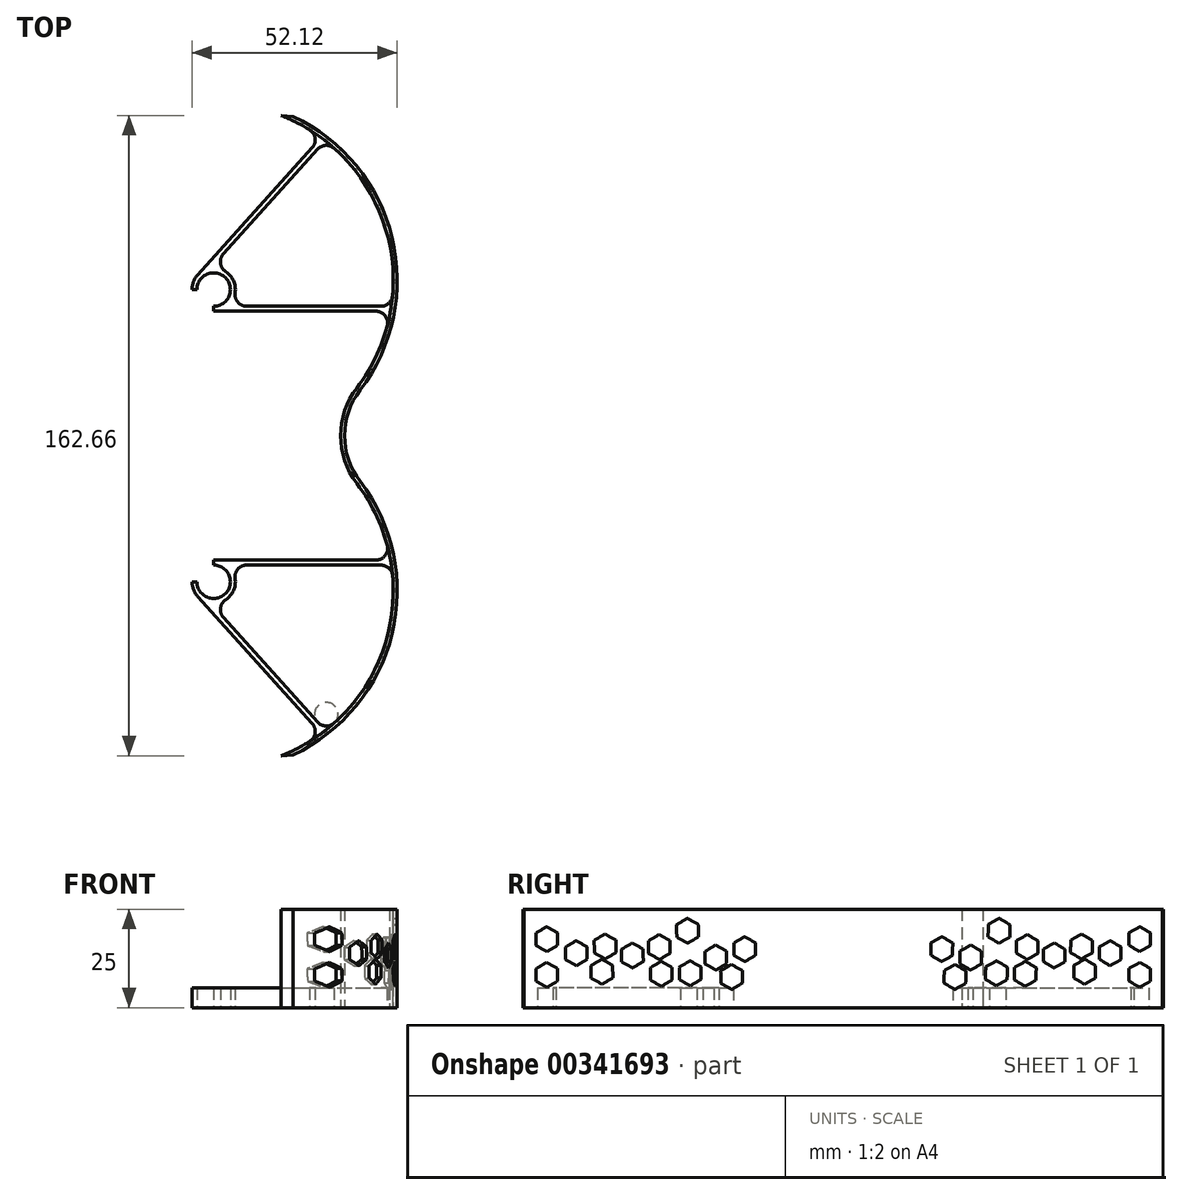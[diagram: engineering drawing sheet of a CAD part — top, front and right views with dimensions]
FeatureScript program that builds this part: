
annotation { "Feature Type Name" : "Feature", "Feature Type Description" : "" }
export const myFeature = defineFeature(function(context is Context, id is Id, definition is map)
    precondition{}
    {
        {
            var Q0;
            Q0=qCreatedBy(makeId("Top.planeOp"),FACE);
            var sketch = newSketch(context, id + "F0", { "sketchPlane" : qUnion([Q0])});
            skCircle(sketch, "E0", {"center": v(0, 0) * mm, "radius": 52.5 * mm, "construction": true});
            skLineSegment(sketch, "E1.bottom", {"start": v(-52.5, 52.5) * mm, "end": v(52.5, 52.5) * mm, "construction": true});
            skLineSegment(sketch, "E1.top", {"start": v(-52.5, -52.5) * mm, "end": v(52.5, -52.5) * mm, "construction": true});
            skLineSegment(sketch, "E1.left", {"start": v(-52.5, 52.5) * mm, "end": v(-52.5, -52.5) * mm, "construction": true});
            skLineSegment(sketch, "E1.right", {"start": v(52.5, 52.5) * mm, "end": v(52.5, -52.5) * mm, "construction": true});
            skLineSegment(sketch, "E2", {"start": v(-52.5, 52.5) * mm, "end": v(52.5, -52.5) * mm, "construction": true});
            skLineSegment(sketch, "E3", {"start": v(52.5, 52.5) * mm, "end": v(-52.5, -52.5) * mm, "construction": true});
            skCircle(sketch, "E4", {"center": v(37.12, -37.12) * mm, "radius": 33 * mm, "construction": true});
            skLineSegment(sketch, "E5.bottom", {"start": v(37.12, -37.12) * mm, "end": v(-37.12, -37.12) * mm, "construction": true});
            skLineSegment(sketch, "E5.top", {"start": v(37.12, 37.12) * mm, "end": v(-37.12, 37.12) * mm, "construction": true});
            skLineSegment(sketch, "E5.left", {"start": v(37.12, -37.12) * mm, "end": v(37.12, 37.12) * mm, "construction": true});
            skLineSegment(sketch, "E5.right", {"start": v(-37.12, -37.12) * mm, "end": v(-37.12, 37.12) * mm, "construction": true});
            skCircle(sketch, "E6", {"center": v(0, -37.12) * mm, "radius": 70 * mm, "construction": true});
            skCircle(sketch, "E7.MirrorC", {"center": v(0, 37.12) * mm, "radius": 70 * mm, "construction": true});
            skArc(sketch, "E8", {"start": v(54.28, -81.33) * mm, "mid": v(57.8, -79.76) * mm, "end": v(61.18, -77.89) * mm});
            skArc(sketch, "E9.MirrorCS", {"start": v(54.28, 81.33) * mm, "mid": v(57.8, 79.76) * mm, "end": v(61.18, 77.89) * mm});
            skPoint(sketch, "E10.visualSharp", {"position": v(59.35, 0) * mm});
            skArc(sketch, "E10.filletArc", {"start": v(73.5, 12.15) * mm, "mid": v(69.38, 0) * mm, "end": v(73.5, -12.15) * mm});
            skArc(sketch, "E11.0", {"start": v(57.33, 81.1) * mm, "mid": v(82.43, 50.37) * mm, "end": v(74.29, 11.54) * mm});
            skArc(sketch, "E11.1", {"start": v(74.29, 11.54) * mm, "mid": v(70.38, 0) * mm, "end": v(74.29, -11.54) * mm});
            skArc(sketch, "E11.2", {"start": v(57.33, -81.1) * mm, "mid": v(82.43, -50.37) * mm, "end": v(74.29, -11.54) * mm});
            skLineSegment(sketch, "E12", {"start": v(54.28, -81.33) * mm, "end": v(57.33, -81.1) * mm});
            skLineSegment(sketch, "E13.MirrorCS", {"start": v(54.28, 81.33) * mm, "end": v(57.33, 81.1) * mm});
            skArc(sketch, "E14.trimOffspring", {"start": v(81.77, -30.15) * mm, "mid": v(78.63, -20.69) * mm, "end": v(73.5, -12.15) * mm});
            skPoint(sketch, "E15.visualSharp", {"position": v(82.51, -34.92) * mm});
            skPoint(sketch, "E16.visualSharp", {"position": v(82.4, -33.91) * mm});
            skArc(sketch, "E17", {"start": v(82.7, -37.69) * mm, "mid": v(82.4, -33.9) * mm, "end": v(81.77, -30.15) * mm});
            skArc(sketch, "E18.trimOffspring", {"start": v(67.26, -73.45) * mm, "mid": v(79.05, -57.33) * mm, "end": v(82.7, -37.69) * mm});
            skPoint(sketch, "E19.visualSharp", {"position": v(64.92, -75.34) * mm});
            skPoint(sketch, "E20.visualSharp", {"position": v(64.12, -75.94) * mm});
            skArc(sketch, "E21", {"start": v(61.18, -77.89) * mm, "mid": v(64.3, -75.79) * mm, "end": v(67.26, -73.45) * mm});
            skArc(sketch, "E22.MirrorCS", {"start": v(82.7, 37.69) * mm, "mid": v(82.65, 36.65) * mm, "end": v(82.58, 35.61) * mm});
            skArc(sketch, "E23.MirrorCS", {"start": v(61.18, 77.89) * mm, "mid": v(61.35, 77.79) * mm, "end": v(61.52, 77.68) * mm});
            skLineSegment(sketch, "E24.trimOffspring", {"start": v(64.1, 75.93) * mm, "end": v(64.12, 75.94) * mm});
            skLineSegment(sketch, "E25.trimOffspring", {"start": v(82.4, 33.91) * mm, "end": v(82.4, 33.91) * mm});
            skArc(sketch, "E26", {"start": v(37.12, 32.87) * mm, "mid": v(40.13, 40.13) * mm, "end": v(32.87, 37.12) * mm});
            skLineSegment(sketch, "E27.0", {"start": v(34.73, 39.33) * mm, "end": v(34.75, 39.35) * mm});
            skArc(sketch, "E28", {"start": v(33.04, 40.8) * mm, "mid": v(31.99, 39.1) * mm, "end": v(31.62, 37.12) * mm});
            skLineSegment(sketch, "E29", {"start": v(37.12, 31.62) * mm, "end": v(78.32, 31.62) * mm});
            skLineSegment(sketch, "E30", {"start": v(45.53, 32.87) * mm, "end": v(79.59, 32.87) * mm});
            skLineSegment(sketch, "E31", {"start": v(33.04, 40.8) * mm, "end": v(62.15, 73.14) * mm});
            skLineSegment(sketch, "E32", {"start": v(39.6, 46.21) * mm, "end": v(63.51, 72.79) * mm});
            skArc(sketch, "E33.trimOffspring", {"start": v(42.56, 36.31) * mm, "mid": v(42.15, 39.36) * mm, "end": v(40.16, 41.7) * mm});
            skArc(sketch, "E34.trimOffspring", {"start": v(67.74, 73.02) * mm, "mid": v(79.18, 57.03) * mm, "end": v(82.7, 37.69) * mm});
            skArc(sketch, "E35.trimOffspring", {"start": v(81.21, 27.85) * mm, "mid": v(78.12, 19.62) * mm, "end": v(73.5, 12.15) * mm});
            skArc(sketch, "E36.filletArc", {"start": v(62.15, 73.14) * mm, "mid": v(62.89, 75.55) * mm, "end": v(61.52, 77.68) * mm});
            skPoint(sketch, "E37.visualSharp", {"position": v(65.45, 74.94) * mm});
            skArc(sketch, "E37.filletArc", {"start": v(67.74, 73.02) * mm, "mid": v(65.58, 73.78) * mm, "end": v(63.51, 72.79) * mm});
            skArc(sketch, "E38.filletArc", {"start": v(79.59, 32.87) * mm, "mid": v(81.61, 33.66) * mm, "end": v(82.58, 35.61) * mm});
            skArc(sketch, "E39.filletArc", {"start": v(81.21, 27.85) * mm, "mid": v(80.7, 30.45) * mm, "end": v(78.32, 31.62) * mm});
            skPoint(sketch, "E40.visualSharp", {"position": v(36.3, 42.56) * mm});
            skArc(sketch, "E40.filletArc", {"start": v(39.6, 46.21) * mm, "mid": v(38.84, 43.83) * mm, "end": v(40.16, 41.7) * mm});
            skPoint(sketch, "E41.visualSharp", {"position": v(40.61, 32.87) * mm});
            skArc(sketch, "E41.filletArc", {"start": v(42.56, 36.31) * mm, "mid": v(43.26, 33.91) * mm, "end": v(45.53, 32.87) * mm});
            skLineSegment(sketch, "E42.MirrorCS", {"start": v(37.12, -31.62) * mm, "end": v(78.32, -31.62) * mm});
            skLineSegment(sketch, "E43.MirrorCS", {"start": v(45.53, -32.87) * mm, "end": v(79.59, -32.87) * mm});
            skArc(sketch, "E44.MirrorCS", {"start": v(81.21, -27.85) * mm, "mid": v(80.7, -30.45) * mm, "end": v(78.32, -31.62) * mm});
            skArc(sketch, "E45.MirrorCS", {"start": v(79.59, -32.87) * mm, "mid": v(81.61, -33.66) * mm, "end": v(82.58, -35.61) * mm});
            skArc(sketch, "E46.MirrorCS", {"start": v(33.04, -40.8) * mm, "mid": v(31.99, -39.1) * mm, "end": v(31.62, -37.12) * mm});
            skArc(sketch, "E47.MirrorC", {"start": v(37.12, -32.87) * mm, "mid": v(40.13, -40.13) * mm, "end": v(32.87, -37.12) * mm});
            skArc(sketch, "E48.MirrorCS", {"start": v(42.56, -36.31) * mm, "mid": v(42.15, -39.36) * mm, "end": v(40.16, -41.7) * mm});
            skArc(sketch, "E49.MirrorCS", {"start": v(39.6, -46.21) * mm, "mid": v(38.84, -43.83) * mm, "end": v(40.16, -41.7) * mm});
            skLineSegment(sketch, "E50.MirrorCS", {"start": v(33.04, -40.8) * mm, "end": v(62.15, -73.14) * mm});
            skArc(sketch, "E51.MirrorCS", {"start": v(67.74, -73.02) * mm, "mid": v(65.58, -73.78) * mm, "end": v(63.51, -72.79) * mm});
            skArc(sketch, "E52.MirrorCS", {"start": v(62.15, -73.14) * mm, "mid": v(62.89, -75.55) * mm, "end": v(61.52, -77.68) * mm});
            skArc(sketch, "E53.MirrorCS", {"start": v(42.56, -36.31) * mm, "mid": v(43.26, -33.91) * mm, "end": v(45.53, -32.87) * mm});
            skLineSegment(sketch, "E54.MirrorCS", {"start": v(39.6, -46.21) * mm, "end": v(63.51, -72.79) * mm});
            skPoint(sketch, "E55.trimOffspring.end.orphan", {"position": v(67.26, 73.45) * mm});
            skArc(sketch, "E56.MirrorCS", {"start": v(81.77, 30.15) * mm, "mid": v(78.63, 20.69) * mm, "end": v(73.5, 12.15) * mm});
            skLineSegment(sketch, "E57", {"start": v(31.62, 37.12) * mm, "end": v(32.87, 37.12) * mm});
            skLineSegment(sketch, "E58", {"start": v(37.12, 32.87) * mm, "end": v(37.12, 31.62) * mm});
            skLineSegment(sketch, "E59", {"start": v(37.12, -31.62) * mm, "end": v(37.12, -32.87) * mm});
            skLineSegment(sketch, "E60", {"start": v(31.62, -37.12) * mm, "end": v(32.87, -37.12) * mm});
            skPoint(sketch, "E61.trimOffspring.end.orphan", {"position": v(37.12, -31.62) * mm});
            skArc(sketch, "E62", {"start": v(81.77, 30.15) * mm, "mid": v(82.2, 32.87) * mm, "end": v(82.58, 35.61) * mm});
            skArc(sketch, "E63", {"start": v(67.74, 73.02) * mm, "mid": v(64.74, 75.49) * mm, "end": v(61.52, 77.68) * mm});
            skSolve(sketch);
        }
        {
            var Q0;
            Q0=makeQuery(id+"F0.imprint","IMPRINT",FACE,{"disambiguationData":[TD([[makeQuery(id+"F0.imprint","IMPRINT",EDGE,{"derivedFrom":sQuery(id+"F0.wireOp",EDGE,"E26")}),-1.0]])]});
            var Q1;
            Q1=makeQuery(id+"F0.imprint","IMPRINT",FACE,{"disambiguationData":[TD([[makeQuery(id+"F0.imprint","IMPRINT",EDGE,{"derivedFrom":sQuery(id+"F0.wireOp",EDGE,"E42.MirrorCS")}),-1.0]])]});
            extrude(context, id + "F1", {"entities" : qUnion([Q0, Q1]), "depth" : 5 * mm});
        }
        {
            var Q0;
            {var subQ5=sQuery(id+"F0.wireOp",EDGE,"E8");Q0=makeQuery(id+"F0.imprint","IMPRINT",FACE,{"disambiguationData":[TD([[makeQuery(id+"F0.imprint","IMPRINT",EDGE,{"derivedFrom":subQ5}),-1.0]])]});}
            extrude(context, id + "F2", {"entities" : qUnion([Q0]), "depth" : 25 * mm});
        }
        {
            var Q0;
            Q0=qCreatedBy(makeId("Right.planeOp"),FACE);
            cPlane(context, id + "F3", {"entities" : qUnion([Q0]), "cplaneType" : CPlaneType.OFFSET, "offset" : 100 * mm, "width" : 150 * mm, "height" : 150 * mm});
        }
        {
            var Q0;
            Q0=qCreatedBy(id+"F3.planeOp",FACE);
            var sketch = newSketch(context, id + "F4", { "sketchPlane" : qUnion([Q0])});
            skCircle(sketch, "E64.cCircle", {"center": v(-67.82, 13.84) * mm, "radius": 2.75 * mm, "construction": true});
            skLineSegment(sketch, "E64.0", {"start": v(-67.87, 17) * mm, "end": v(-65.1, 15.47) * mm});
            skLineSegment(sketch, "E64.1", {"start": v(-65.1, 15.47) * mm, "end": v(-65.04, 12.3) * mm});
            skLineSegment(sketch, "E64.2", {"start": v(-65.04, 12.3) * mm, "end": v(-67.76, 10.67) * mm});
            skLineSegment(sketch, "E64.3", {"start": v(-67.76, 10.67) * mm, "end": v(-70.54, 12.2) * mm});
            skLineSegment(sketch, "E64.4", {"start": v(-70.54, 12.2) * mm, "end": v(-70.59, 15.38) * mm});
            skLineSegment(sketch, "E64.5", {"start": v(-70.59, 15.38) * mm, "end": v(-67.87, 17) * mm});
            skPoint(sketch, "E64.0.midPoint", {"position": v(-66.48, 16.24) * mm});
            skCircle(sketch, "E65.cCircle", {"center": v(-60.51, 15.54) * mm, "radius": 2.75 * mm, "construction": true});
            skLineSegment(sketch, "E65.0", {"start": v(-60.57, 18.7) * mm, "end": v(-57.8, 17.17) * mm});
            skLineSegment(sketch, "E65.1", {"start": v(-57.8, 17.17) * mm, "end": v(-57.74, 14) * mm});
            skLineSegment(sketch, "E65.2", {"start": v(-57.74, 14) * mm, "end": v(-60.46, 12.37) * mm});
            skLineSegment(sketch, "E65.3", {"start": v(-60.46, 12.37) * mm, "end": v(-63.23, 13.9) * mm});
            skLineSegment(sketch, "E65.4", {"start": v(-63.23, 13.9) * mm, "end": v(-63.29, 17.08) * mm});
            skLineSegment(sketch, "E65.5", {"start": v(-63.29, 17.08) * mm, "end": v(-60.57, 18.7) * mm});
            skPoint(sketch, "E65.0.midPoint", {"position": v(-59.18, 17.94) * mm});
            skCircle(sketch, "E66.cCircle", {"center": v(-53.58, 13.27) * mm, "radius": 2.75 * mm, "construction": true});
            skLineSegment(sketch, "E66.0", {"start": v(-53.63, 16.44) * mm, "end": v(-50.86, 14.9) * mm});
            skLineSegment(sketch, "E66.1", {"start": v(-50.86, 14.9) * mm, "end": v(-50.8, 11.73) * mm});
            skLineSegment(sketch, "E66.2", {"start": v(-50.8, 11.73) * mm, "end": v(-53.53, 10.1) * mm});
            skLineSegment(sketch, "E66.3", {"start": v(-53.53, 10.1) * mm, "end": v(-56.3, 11.64) * mm});
            skLineSegment(sketch, "E66.4", {"start": v(-56.3, 11.64) * mm, "end": v(-56.35, 14.81) * mm});
            skLineSegment(sketch, "E66.5", {"start": v(-56.35, 14.81) * mm, "end": v(-53.63, 16.44) * mm});
            skPoint(sketch, "E66.0.midPoint", {"position": v(-52.24, 15.67) * mm});
            skCircle(sketch, "E67.cCircle", {"center": v(-46.74, 15.4) * mm, "radius": 2.75 * mm, "construction": true});
            skLineSegment(sketch, "E67.0", {"start": v(-46.8, 18.58) * mm, "end": v(-44.02, 17.04) * mm});
            skLineSegment(sketch, "E67.1", {"start": v(-44.02, 17.04) * mm, "end": v(-43.97, 13.86) * mm});
            skLineSegment(sketch, "E67.2", {"start": v(-43.97, 13.86) * mm, "end": v(-46.69, 12.23) * mm});
            skLineSegment(sketch, "E67.3", {"start": v(-46.69, 12.23) * mm, "end": v(-49.46, 13.77) * mm});
            skLineSegment(sketch, "E67.4", {"start": v(-49.46, 13.77) * mm, "end": v(-49.51, 16.94) * mm});
            skLineSegment(sketch, "E67.5", {"start": v(-49.51, 16.94) * mm, "end": v(-46.8, 18.58) * mm});
            skPoint(sketch, "E67.0.midPoint", {"position": v(-45.4, 17.8) * mm});
            skCircle(sketch, "E68.cCircle", {"center": v(-38.9, 8.74) * mm, "radius": 2.75 * mm, "construction": true});
            skLineSegment(sketch, "E68.0", {"start": v(-38.96, 11.9) * mm, "end": v(-36.19, 10.37) * mm});
            skLineSegment(sketch, "E68.1", {"start": v(-36.19, 10.37) * mm, "end": v(-36.13, 7.2) * mm});
            skLineSegment(sketch, "E68.2", {"start": v(-36.13, 7.2) * mm, "end": v(-38.85, 5.57) * mm});
            skLineSegment(sketch, "E68.3", {"start": v(-38.85, 5.57) * mm, "end": v(-41.63, 7.1) * mm});
            skLineSegment(sketch, "E68.4", {"start": v(-41.63, 7.1) * mm, "end": v(-41.68, 10.28) * mm});
            skLineSegment(sketch, "E68.5", {"start": v(-41.68, 10.28) * mm, "end": v(-38.96, 11.9) * mm});
            skPoint(sketch, "E68.0.midPoint", {"position": v(-37.57, 11.14) * mm});
            skCircle(sketch, "E69.cCircle", {"center": v(-32.38, 12.74) * mm, "radius": 2.75 * mm, "construction": true});
            skLineSegment(sketch, "E69.0", {"start": v(-32.43, 15.9) * mm, "end": v(-29.66, 14.37) * mm});
            skLineSegment(sketch, "E69.1", {"start": v(-29.66, 14.37) * mm, "end": v(-29.6, 11.2) * mm});
            skLineSegment(sketch, "E69.2", {"start": v(-29.6, 11.2) * mm, "end": v(-32.32, 9.57) * mm});
            skLineSegment(sketch, "E69.3", {"start": v(-32.32, 9.57) * mm, "end": v(-35.1, 11.1) * mm});
            skLineSegment(sketch, "E69.4", {"start": v(-35.1, 11.1) * mm, "end": v(-35.15, 14.28) * mm});
            skLineSegment(sketch, "E69.5", {"start": v(-35.15, 14.28) * mm, "end": v(-32.43, 15.9) * mm});
            skPoint(sketch, "E69.0.midPoint", {"position": v(-31.04, 15.14) * mm});
            skCircle(sketch, "E70.cCircle", {"center": v(-39.57, 19.54) * mm, "radius": 2.75 * mm, "construction": true});
            skLineSegment(sketch, "E70.0", {"start": v(-39.63, 22.71) * mm, "end": v(-36.85, 21.17) * mm});
            skLineSegment(sketch, "E70.1", {"start": v(-36.85, 21.17) * mm, "end": v(-36.8, 18) * mm});
            skLineSegment(sketch, "E70.2", {"start": v(-36.8, 18) * mm, "end": v(-39.52, 16.37) * mm});
            skLineSegment(sketch, "E70.3", {"start": v(-39.52, 16.37) * mm, "end": v(-42.3, 17.9) * mm});
            skLineSegment(sketch, "E70.4", {"start": v(-42.3, 17.9) * mm, "end": v(-42.35, 21.08) * mm});
            skLineSegment(sketch, "E70.5", {"start": v(-42.35, 21.08) * mm, "end": v(-39.63, 22.71) * mm});
            skPoint(sketch, "E70.0.midPoint", {"position": v(-38.24, 21.94) * mm});
            skCircle(sketch, "E71.cCircle", {"center": v(-25.04, 14.87) * mm, "radius": 2.75 * mm, "construction": true});
            skLineSegment(sketch, "E71.0", {"start": v(-25.09, 18.04) * mm, "end": v(-22.32, 16.5) * mm});
            skLineSegment(sketch, "E71.1", {"start": v(-22.32, 16.5) * mm, "end": v(-22.26, 13.33) * mm});
            skLineSegment(sketch, "E71.2", {"start": v(-22.26, 13.33) * mm, "end": v(-24.98, 11.7) * mm});
            skLineSegment(sketch, "E71.3", {"start": v(-24.98, 11.7) * mm, "end": v(-27.75, 13.24) * mm});
            skLineSegment(sketch, "E71.4", {"start": v(-27.75, 13.24) * mm, "end": v(-27.8, 16.41) * mm});
            skLineSegment(sketch, "E71.5", {"start": v(-27.8, 16.41) * mm, "end": v(-25.09, 18.04) * mm});
            skPoint(sketch, "E71.0.midPoint", {"position": v(-23.7, 17.27) * mm});
            skCircle(sketch, "E72.cCircle", {"center": v(-61.31, 9.14) * mm, "radius": 2.75 * mm, "construction": true});
            skLineSegment(sketch, "E72.0", {"start": v(-61.37, 12.3) * mm, "end": v(-58.6, 10.77) * mm});
            skLineSegment(sketch, "E72.1", {"start": v(-58.6, 10.77) * mm, "end": v(-58.54, 7.6) * mm});
            skLineSegment(sketch, "E72.2", {"start": v(-58.54, 7.6) * mm, "end": v(-61.26, 5.97) * mm});
            skLineSegment(sketch, "E72.3", {"start": v(-61.26, 5.97) * mm, "end": v(-64.03, 7.5) * mm});
            skLineSegment(sketch, "E72.4", {"start": v(-64.03, 7.5) * mm, "end": v(-64.09, 10.68) * mm});
            skLineSegment(sketch, "E72.5", {"start": v(-64.09, 10.68) * mm, "end": v(-61.37, 12.3) * mm});
            skPoint(sketch, "E72.0.midPoint", {"position": v(-59.98, 11.54) * mm});
            skCircle(sketch, "E73.cCircle", {"center": v(-46.24, 8.6) * mm, "radius": 2.75 * mm, "construction": true});
            skLineSegment(sketch, "E73.0", {"start": v(-46.3, 11.77) * mm, "end": v(-43.52, 10.23) * mm});
            skLineSegment(sketch, "E73.1", {"start": v(-43.52, 10.23) * mm, "end": v(-43.47, 7.06) * mm});
            skLineSegment(sketch, "E73.2", {"start": v(-43.47, 7.06) * mm, "end": v(-46.19, 5.43) * mm});
            skLineSegment(sketch, "E73.3", {"start": v(-46.19, 5.43) * mm, "end": v(-48.96, 6.97) * mm});
            skLineSegment(sketch, "E73.4", {"start": v(-48.96, 6.97) * mm, "end": v(-49.01, 10.14) * mm});
            skLineSegment(sketch, "E73.5", {"start": v(-49.01, 10.14) * mm, "end": v(-46.3, 11.77) * mm});
            skPoint(sketch, "E73.0.midPoint", {"position": v(-44.9, 11) * mm});
            skCircle(sketch, "E74.cCircle", {"center": v(-75.32, 8.34) * mm, "radius": 2.75 * mm, "construction": true});
            skLineSegment(sketch, "E74.0", {"start": v(-75.37, 11.5) * mm, "end": v(-72.6, 9.97) * mm});
            skLineSegment(sketch, "E74.1", {"start": v(-72.6, 9.97) * mm, "end": v(-72.55, 6.8) * mm});
            skLineSegment(sketch, "E74.2", {"start": v(-72.55, 6.8) * mm, "end": v(-75.27, 5.17) * mm});
            skLineSegment(sketch, "E74.3", {"start": v(-75.27, 5.17) * mm, "end": v(-78.04, 6.7) * mm});
            skLineSegment(sketch, "E74.4", {"start": v(-78.04, 6.7) * mm, "end": v(-78.1, 9.88) * mm});
            skLineSegment(sketch, "E74.5", {"start": v(-78.1, 9.88) * mm, "end": v(-75.37, 11.5) * mm});
            skPoint(sketch, "E74.0.midPoint", {"position": v(-73.98, 10.74) * mm});
            skCircle(sketch, "E75.cCircle", {"center": v(-28.37, 7.8) * mm, "radius": 2.75 * mm, "construction": true});
            skLineSegment(sketch, "E75.0", {"start": v(-28.42, 10.97) * mm, "end": v(-25.65, 9.43) * mm});
            skLineSegment(sketch, "E75.1", {"start": v(-25.65, 9.43) * mm, "end": v(-25.6, 6.26) * mm});
            skLineSegment(sketch, "E75.2", {"start": v(-25.6, 6.26) * mm, "end": v(-28.32, 4.63) * mm});
            skLineSegment(sketch, "E75.3", {"start": v(-28.32, 4.63) * mm, "end": v(-31.09, 6.17) * mm});
            skLineSegment(sketch, "E75.4", {"start": v(-31.09, 6.17) * mm, "end": v(-31.14, 9.34) * mm});
            skLineSegment(sketch, "E75.5", {"start": v(-31.14, 9.34) * mm, "end": v(-28.42, 10.97) * mm});
            skPoint(sketch, "E75.0.midPoint", {"position": v(-27.04, 10.2) * mm});
            skCircle(sketch, "E76.cCircle", {"center": v(-75.32, 17.4) * mm, "radius": 2.75 * mm, "construction": true});
            skLineSegment(sketch, "E76.0", {"start": v(-75.37, 20.58) * mm, "end": v(-72.6, 19.04) * mm});
            skLineSegment(sketch, "E76.1", {"start": v(-72.6, 19.04) * mm, "end": v(-72.55, 15.87) * mm});
            skLineSegment(sketch, "E76.2", {"start": v(-72.55, 15.87) * mm, "end": v(-75.27, 14.23) * mm});
            skLineSegment(sketch, "E76.3", {"start": v(-75.27, 14.23) * mm, "end": v(-78.04, 15.77) * mm});
            skLineSegment(sketch, "E76.4", {"start": v(-78.04, 15.77) * mm, "end": v(-78.1, 18.95) * mm});
            skLineSegment(sketch, "E76.5", {"start": v(-78.1, 18.95) * mm, "end": v(-75.37, 20.58) * mm});
            skPoint(sketch, "E76.0.midPoint", {"position": v(-73.98, 19.8) * mm});
            skLineSegment(sketch, "E77.MirrorCS", {"start": v(36.13, 7.2) * mm, "end": v(38.85, 5.57) * mm});
            skLineSegment(sketch, "E78.MirrorCS", {"start": v(61.37, 12.3) * mm, "end": v(58.6, 10.77) * mm});
            skLineSegment(sketch, "E79.MirrorCS", {"start": v(49.46, 13.77) * mm, "end": v(49.51, 16.94) * mm});
            skLineSegment(sketch, "E80.MirrorCS", {"start": v(29.6, 11.2) * mm, "end": v(32.32, 9.57) * mm});
            skLineSegment(sketch, "E81.MirrorCS", {"start": v(50.86, 14.9) * mm, "end": v(50.8, 11.73) * mm});
            skLineSegment(sketch, "E82.MirrorCS", {"start": v(70.59, 15.38) * mm, "end": v(67.87, 17) * mm});
            skLineSegment(sketch, "E83.MirrorCS", {"start": v(35.1, 11.1) * mm, "end": v(35.15, 14.28) * mm});
            skCircle(sketch, "E84.MirrorC", {"center": v(46.74, 15.4) * mm, "radius": 2.75 * mm, "construction": true});
            skLineSegment(sketch, "E85.MirrorCS", {"start": v(39.63, 22.71) * mm, "end": v(36.85, 21.17) * mm});
            skLineSegment(sketch, "E86.MirrorCS", {"start": v(43.97, 13.86) * mm, "end": v(46.69, 12.23) * mm});
            skLineSegment(sketch, "E87.MirrorCS", {"start": v(29.66, 14.37) * mm, "end": v(29.6, 11.2) * mm});
            skLineSegment(sketch, "E88.MirrorCS", {"start": v(31.14, 9.34) * mm, "end": v(28.42, 10.97) * mm});
            skCircle(sketch, "E89.MirrorC", {"center": v(61.31, 9.14) * mm, "radius": 2.75 * mm, "construction": true});
            skLineSegment(sketch, "E90.MirrorCS", {"start": v(67.76, 10.67) * mm, "end": v(70.54, 12.2) * mm});
            skLineSegment(sketch, "E91.MirrorCS", {"start": v(24.98, 11.7) * mm, "end": v(27.75, 13.24) * mm});
            skLineSegment(sketch, "E92.MirrorCS", {"start": v(48.96, 6.97) * mm, "end": v(49.01, 10.14) * mm});
            skLineSegment(sketch, "E93.MirrorCS", {"start": v(32.32, 9.57) * mm, "end": v(35.1, 11.1) * mm});
            skCircle(sketch, "E94.MirrorC", {"center": v(39.57, 19.54) * mm, "radius": 2.75 * mm, "construction": true});
            skCircle(sketch, "E95.MirrorC", {"center": v(38.9, 8.74) * mm, "radius": 2.75 * mm, "construction": true});
            skLineSegment(sketch, "E96.MirrorCS", {"start": v(53.53, 10.1) * mm, "end": v(56.3, 11.64) * mm});
            skCircle(sketch, "E97.MirrorC", {"center": v(53.58, 13.27) * mm, "radius": 2.75 * mm, "construction": true});
            skLineSegment(sketch, "E98.MirrorCS", {"start": v(72.6, 9.97) * mm, "end": v(72.55, 6.8) * mm});
            skLineSegment(sketch, "E99.MirrorCS", {"start": v(43.47, 7.06) * mm, "end": v(46.19, 5.43) * mm});
            skLineSegment(sketch, "E100.MirrorCS", {"start": v(57.8, 17.17) * mm, "end": v(57.74, 14) * mm});
            skLineSegment(sketch, "E101.MirrorCS", {"start": v(25.09, 18.04) * mm, "end": v(22.32, 16.5) * mm});
            skLineSegment(sketch, "E102.MirrorCS", {"start": v(39.52, 16.37) * mm, "end": v(42.3, 17.9) * mm});
            skCircle(sketch, "E103.MirrorC", {"center": v(60.51, 15.54) * mm, "radius": 2.75 * mm, "construction": true});
            skLineSegment(sketch, "E104.MirrorCS", {"start": v(56.3, 11.64) * mm, "end": v(56.35, 14.81) * mm});
            skCircle(sketch, "E105.MirrorC", {"center": v(67.82, 13.84) * mm, "radius": 2.75 * mm, "construction": true});
            skLineSegment(sketch, "E106.MirrorCS", {"start": v(65.1, 15.47) * mm, "end": v(65.04, 12.3) * mm});
            skLineSegment(sketch, "E107.MirrorCS", {"start": v(27.75, 13.24) * mm, "end": v(27.8, 16.41) * mm});
            skLineSegment(sketch, "E108.MirrorCS", {"start": v(42.3, 17.9) * mm, "end": v(42.35, 21.08) * mm});
            skLineSegment(sketch, "E109.MirrorCS", {"start": v(31.09, 6.17) * mm, "end": v(31.14, 9.34) * mm});
            skLineSegment(sketch, "E110.MirrorCS", {"start": v(64.03, 7.5) * mm, "end": v(64.09, 10.68) * mm});
            skLineSegment(sketch, "E111.MirrorCS", {"start": v(60.57, 18.7) * mm, "end": v(57.8, 17.17) * mm});
            skLineSegment(sketch, "E112.MirrorCS", {"start": v(72.55, 6.8) * mm, "end": v(75.27, 5.17) * mm});
            skCircle(sketch, "E113.MirrorC", {"center": v(32.38, 12.74) * mm, "radius": 2.75 * mm, "construction": true});
            skLineSegment(sketch, "E114.MirrorCS", {"start": v(36.85, 21.17) * mm, "end": v(36.8, 18) * mm});
            skLineSegment(sketch, "E115.MirrorCS", {"start": v(75.37, 11.5) * mm, "end": v(72.6, 9.97) * mm});
            skLineSegment(sketch, "E116.MirrorCS", {"start": v(44.02, 17.04) * mm, "end": v(43.97, 13.86) * mm});
            skLineSegment(sketch, "E117.MirrorCS", {"start": v(60.46, 12.37) * mm, "end": v(63.23, 13.9) * mm});
            skCircle(sketch, "E118.MirrorC", {"center": v(28.37, 7.8) * mm, "radius": 2.75 * mm, "construction": true});
            skLineSegment(sketch, "E119.MirrorCS", {"start": v(46.3, 11.77) * mm, "end": v(43.52, 10.23) * mm});
            skLineSegment(sketch, "E120.MirrorCS", {"start": v(58.6, 10.77) * mm, "end": v(58.54, 7.6) * mm});
            skLineSegment(sketch, "E121.MirrorCS", {"start": v(46.19, 5.43) * mm, "end": v(48.96, 6.97) * mm});
            skLineSegment(sketch, "E122.MirrorCS", {"start": v(25.6, 6.26) * mm, "end": v(28.32, 4.63) * mm});
            skLineSegment(sketch, "E123.MirrorCS", {"start": v(50.8, 11.73) * mm, "end": v(53.53, 10.1) * mm});
            skLineSegment(sketch, "E124.MirrorCS", {"start": v(57.74, 14) * mm, "end": v(60.46, 12.37) * mm});
            skLineSegment(sketch, "E125.MirrorCS", {"start": v(36.19, 10.37) * mm, "end": v(36.13, 7.2) * mm});
            skLineSegment(sketch, "E126.MirrorCS", {"start": v(70.54, 12.2) * mm, "end": v(70.59, 15.38) * mm});
            skLineSegment(sketch, "E127.MirrorCS", {"start": v(28.32, 4.63) * mm, "end": v(31.09, 6.17) * mm});
            skLineSegment(sketch, "E128.MirrorCS", {"start": v(65.04, 12.3) * mm, "end": v(67.76, 10.67) * mm});
            skLineSegment(sketch, "E129.MirrorCS", {"start": v(58.54, 7.6) * mm, "end": v(61.26, 5.97) * mm});
            skLineSegment(sketch, "E130.MirrorCS", {"start": v(41.68, 10.28) * mm, "end": v(38.96, 11.9) * mm});
            skLineSegment(sketch, "E131.MirrorCS", {"start": v(36.8, 18) * mm, "end": v(39.52, 16.37) * mm});
            skLineSegment(sketch, "E132.MirrorCS", {"start": v(25.65, 9.43) * mm, "end": v(25.6, 6.26) * mm});
            skLineSegment(sketch, "E133.MirrorCS", {"start": v(72.6, 19.04) * mm, "end": v(72.55, 15.87) * mm});
            skCircle(sketch, "E134.MirrorC", {"center": v(25.04, 14.87) * mm, "radius": 2.75 * mm, "construction": true});
            skLineSegment(sketch, "E135.MirrorCS", {"start": v(63.29, 17.08) * mm, "end": v(60.57, 18.7) * mm});
            skLineSegment(sketch, "E136.MirrorCS", {"start": v(38.85, 5.57) * mm, "end": v(41.63, 7.1) * mm});
            skLineSegment(sketch, "E137.MirrorCS", {"start": v(49.51, 16.94) * mm, "end": v(46.8, 18.58) * mm});
            skLineSegment(sketch, "E138.MirrorCS", {"start": v(22.26, 13.33) * mm, "end": v(24.98, 11.7) * mm});
            skLineSegment(sketch, "E139.MirrorCS", {"start": v(64.09, 10.68) * mm, "end": v(61.37, 12.3) * mm});
            skLineSegment(sketch, "E140.MirrorCS", {"start": v(49.01, 10.14) * mm, "end": v(46.3, 11.77) * mm});
            skLineSegment(sketch, "E141.MirrorCS", {"start": v(28.42, 10.97) * mm, "end": v(25.65, 9.43) * mm});
            skLineSegment(sketch, "E142.MirrorCS", {"start": v(63.23, 13.9) * mm, "end": v(63.29, 17.08) * mm});
            skLineSegment(sketch, "E143.MirrorCS", {"start": v(27.8, 16.41) * mm, "end": v(25.09, 18.04) * mm});
            skLineSegment(sketch, "E144.MirrorCS", {"start": v(61.26, 5.97) * mm, "end": v(64.03, 7.5) * mm});
            skLineSegment(sketch, "E145.MirrorCS", {"start": v(32.43, 15.9) * mm, "end": v(29.66, 14.37) * mm});
            skLineSegment(sketch, "E146.MirrorCS", {"start": v(75.37, 20.58) * mm, "end": v(72.6, 19.04) * mm});
            skLineSegment(sketch, "E147.MirrorCS", {"start": v(78.1, 18.95) * mm, "end": v(75.37, 20.58) * mm});
            skLineSegment(sketch, "E148.MirrorCS", {"start": v(22.32, 16.5) * mm, "end": v(22.26, 13.33) * mm});
            skLineSegment(sketch, "E149.MirrorCS", {"start": v(42.35, 21.08) * mm, "end": v(39.63, 22.71) * mm});
            skLineSegment(sketch, "E150.MirrorCS", {"start": v(67.87, 17) * mm, "end": v(65.1, 15.47) * mm});
            skLineSegment(sketch, "E151.MirrorCS", {"start": v(43.52, 10.23) * mm, "end": v(43.47, 7.06) * mm});
            skLineSegment(sketch, "E152.MirrorCS", {"start": v(38.96, 11.9) * mm, "end": v(36.19, 10.37) * mm});
            skLineSegment(sketch, "E153.MirrorCS", {"start": v(53.63, 16.44) * mm, "end": v(50.86, 14.9) * mm});
            skLineSegment(sketch, "E154.MirrorCS", {"start": v(41.63, 7.1) * mm, "end": v(41.68, 10.28) * mm});
            skLineSegment(sketch, "E155.MirrorCS", {"start": v(46.8, 18.58) * mm, "end": v(44.02, 17.04) * mm});
            skLineSegment(sketch, "E156.MirrorCS", {"start": v(56.35, 14.81) * mm, "end": v(53.63, 16.44) * mm});
            skLineSegment(sketch, "E157.MirrorCS", {"start": v(46.69, 12.23) * mm, "end": v(49.46, 13.77) * mm});
            skLineSegment(sketch, "E158.MirrorCS", {"start": v(72.55, 15.87) * mm, "end": v(75.27, 14.23) * mm});
            skLineSegment(sketch, "E159.MirrorCS", {"start": v(35.15, 14.28) * mm, "end": v(32.43, 15.9) * mm});
            skCircle(sketch, "E160.MirrorC", {"center": v(46.24, 8.6) * mm, "radius": 2.75 * mm, "construction": true});
            skPoint(sketch, "E161.MirrorP", {"position": v(37.57, 11.14) * mm});
            skPoint(sketch, "E162.MirrorP", {"position": v(66.48, 16.24) * mm});
            skPoint(sketch, "E163.MirrorP", {"position": v(59.98, 11.54) * mm});
            skPoint(sketch, "E164.MirrorP", {"position": v(45.4, 17.8) * mm});
            skPoint(sketch, "E165.MirrorP", {"position": v(44.9, 11) * mm});
            skPoint(sketch, "E166.MirrorP", {"position": v(31.04, 15.14) * mm});
            skCircle(sketch, "E167.MirrorC", {"center": v(75.32, 17.4) * mm, "radius": 2.75 * mm, "construction": true});
            skPoint(sketch, "E168.MirrorP", {"position": v(73.98, 10.74) * mm});
            skPoint(sketch, "E169.MirrorP", {"position": v(27.04, 10.2) * mm});
            skPoint(sketch, "E170.MirrorP", {"position": v(38.24, 21.94) * mm});
            skPoint(sketch, "E171.MirrorP", {"position": v(59.18, 17.94) * mm});
            skPoint(sketch, "E172.MirrorP", {"position": v(23.7, 17.27) * mm});
            skPoint(sketch, "E173.MirrorP", {"position": v(73.98, 19.8) * mm});
            skPoint(sketch, "E174.MirrorP", {"position": v(52.24, 15.67) * mm});
            skLineSegment(sketch, "E175.MirrorCS", {"start": v(78.1, 9.88) * mm, "end": v(75.37, 11.5) * mm});
            skLineSegment(sketch, "E176.MirrorCS", {"start": v(78.04, 6.7) * mm, "end": v(78.1, 9.88) * mm});
            skCircle(sketch, "E177.MirrorC", {"center": v(75.32, 8.34) * mm, "radius": 2.75 * mm, "construction": true});
            skLineSegment(sketch, "E178.MirrorCS", {"start": v(75.27, 5.17) * mm, "end": v(78.04, 6.7) * mm});
            skLineSegment(sketch, "E179.MirrorCS", {"start": v(78.04, 15.77) * mm, "end": v(78.1, 18.95) * mm});
            skLineSegment(sketch, "E180.MirrorCS", {"start": v(75.27, 14.23) * mm, "end": v(78.04, 15.77) * mm});
            skSolve(sketch);
        }
        {
            var Q0;
            Q0 = qSketchRegion(id + "F4", true);
            extrude(context, id + "F5", {"entities" : qUnion([Q0]), "operationType" : NewBodyOperationType.REMOVE, "oppositeDirection" : true, "depth" : 50 * mm});
        }
    });
